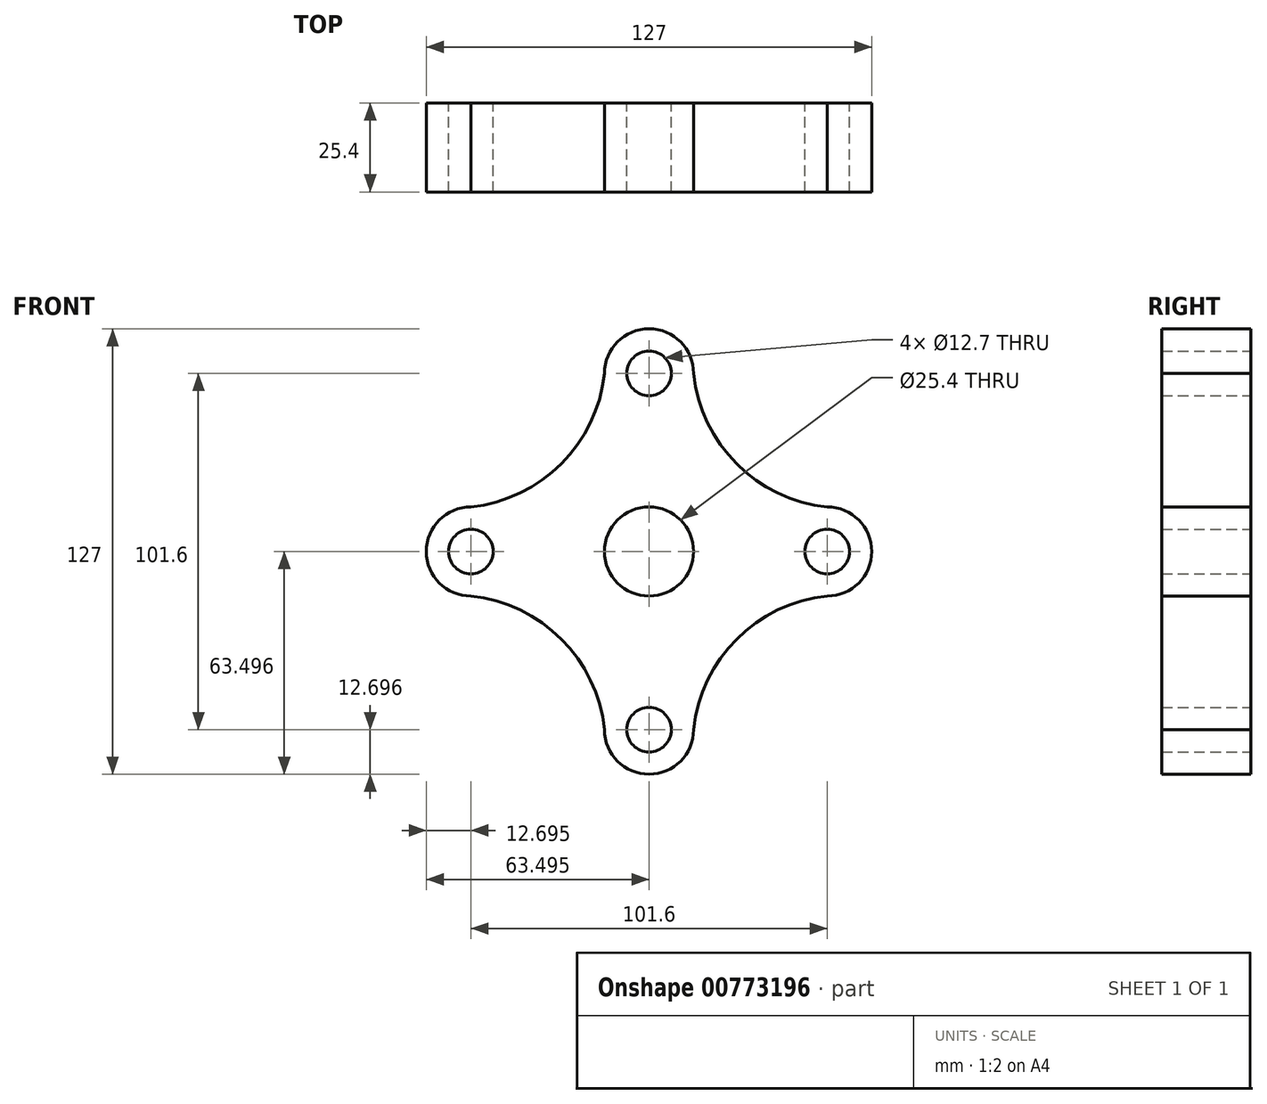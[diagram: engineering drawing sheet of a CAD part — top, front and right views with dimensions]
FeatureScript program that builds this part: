
annotation { "Feature Type Name" : "Feature", "Feature Type Description" : "" }
export const myFeature = defineFeature(function(context is Context, id is Id, definition is map)
    precondition{}
    {
        {
            var Q0;
            Q0=qCreatedBy(makeId("Front.planeOp"),FACE);
            var sketch = newSketch(context, id + "F0", { "sketchPlane" : qUnion([Q0])});
            skCircle(sketch, "E0", {"center": v(-51.08, 0.48) * mm, "radius": 6.35 * mm});
            skCircle(sketch, "E1", {"center": v(50.52, 0.48) * mm, "radius": 6.35 * mm});
            skCircle(sketch, "E2", {"center": v(-0.28, 0.48) * mm, "radius": 12.7 * mm});
            skCircle(sketch, "E3", {"center": v(-0.28, -50.32) * mm, "radius": 6.35 * mm});
            skCircle(sketch, "E4", {"center": v(-0.28, 51.28) * mm, "radius": 6.35 * mm});
            skArc(sketch, "E5", {"start": v(-51.08, 13.18) * mm, "mid": v(-25.31, 25.5) * mm, "end": v(-12.98, 51.28) * mm});
            skArc(sketch, "E6", {"start": v(12.42, 51.28) * mm, "mid": v(-0.28, 63.98) * mm, "end": v(-12.98, 51.28) * mm});
            skArc(sketch, "E7", {"start": v(-51.08, 13.18) * mm, "mid": v(-63.78, 0.48) * mm, "end": v(-51.08, -12.22) * mm});
            skPoint(sketch, "E8.trimOffspring.end.orphan", {"position": v(-51.08, 51.28) * mm});
            skArc(sketch, "E9", {"start": v(12.42, 51.28) * mm, "mid": v(24.7, 25.46) * mm, "end": v(50.52, 13.18) * mm});
            skArc(sketch, "E10", {"start": v(50.52, -12.22) * mm, "mid": v(63.22, 0.48) * mm, "end": v(50.52, 13.18) * mm});
            skPoint(sketch, "E11.orphan", {"position": v(50.52, 51.28) * mm});
            skArc(sketch, "E12", {"start": v(50.52, -12.22) * mm, "mid": v(24.7, -24.5) * mm, "end": v(12.42, -50.32) * mm});
            skArc(sketch, "E13", {"start": v(-12.98, -50.32) * mm, "mid": v(-0.28, -63.02) * mm, "end": v(12.42, -50.32) * mm});
            skArc(sketch, "E14", {"start": v(-12.98, -50.32) * mm, "mid": v(-25.27, -24.5) * mm, "end": v(-51.08, -12.22) * mm});
            skPoint(sketch, "E15.orphan", {"position": v(-51.08, -50.32) * mm});
            skPoint(sketch, "E16.orphan", {"position": v(50.52, -50.32) * mm});
            skSolve(sketch);
        }
        {
            var Q0;
            Q0=qSketchRegion(id+"F0",true);
            extrude(context, id + "F1", {"entities" : qUnion([Q0]), "depth" : 25.4 * mm, "offsetDistance" : 25.4 * mm});
        }
    });
